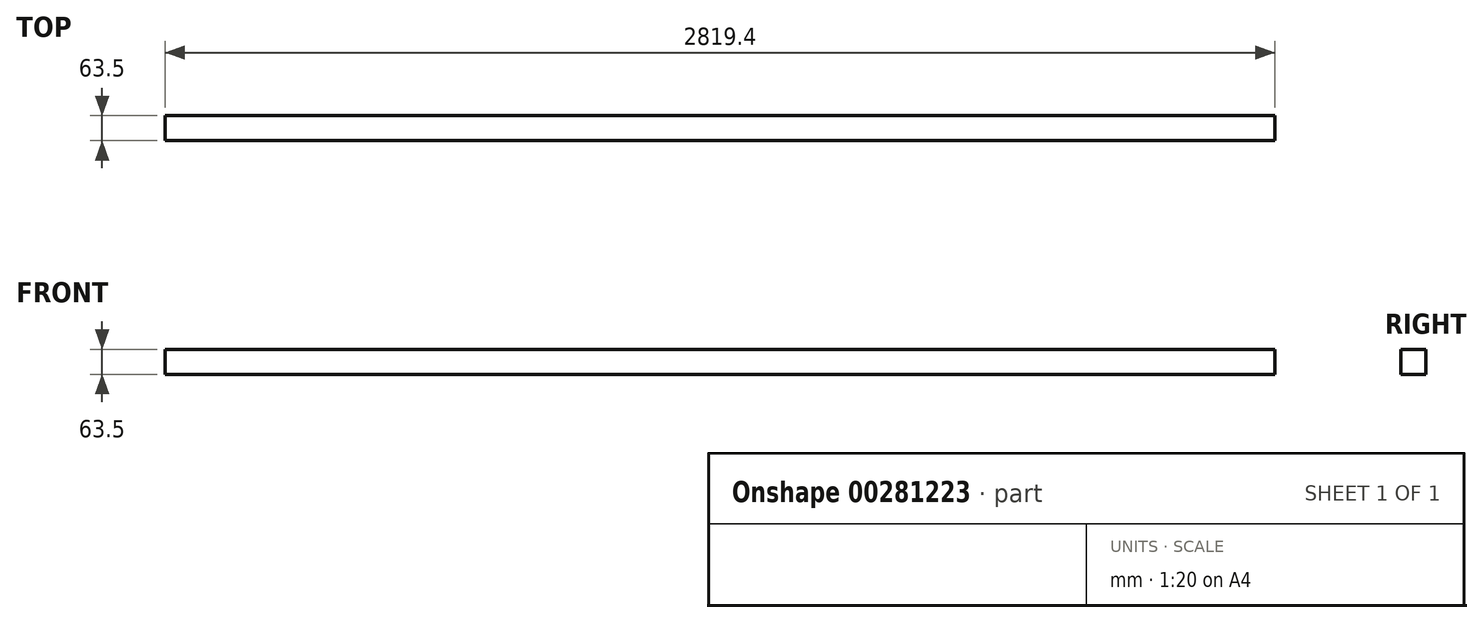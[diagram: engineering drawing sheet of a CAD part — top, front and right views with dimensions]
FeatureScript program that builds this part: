
annotation { "Feature Type Name" : "Feature", "Feature Type Description" : "" }
export const myFeature = defineFeature(function(context is Context, id is Id, definition is map)
    precondition{}
    {
        {
            var Q0;
            Q0=qCreatedBy(makeId("Right.planeOp"),FACE);
            var sketch = newSketch(context, id + "F0", { "sketchPlane" : qUnion([Q0])});
            skLineSegment(sketch, "E0.bottom", {"start": v(-31.75, 31.75) * mm, "end": v(31.75, 31.75) * mm});
            skLineSegment(sketch, "E0.top", {"start": v(-31.75, -31.75) * mm, "end": v(31.75, -31.75) * mm});
            skLineSegment(sketch, "E0.left", {"start": v(-31.75, 31.75) * mm, "end": v(-31.75, -31.75) * mm});
            skLineSegment(sketch, "E0.right", {"start": v(31.75, 31.75) * mm, "end": v(31.75, -31.75) * mm});
            skPoint(sketch, "E0.middle", {"position": v(0, 0) * mm});
            skSolve(sketch);
        }
        {
            var Q0;
            Q0=makeQuery(id+"F0.imprint","IMPRINT",FACE,{"disambiguationData":[TD([[makeQuery(id+"F0.imprint","IMPRINT",EDGE,{"derivedFrom":sQuery(id+"F0.wireOp",EDGE,"E0.bottom")}),-1.0]])]});
            extrude(context, id + "F1", {"entities" : qUnion([Q0]), "endBound" : BoundingType.SYMMETRIC, "depth" : 2819.4 * mm});
        }
    });
